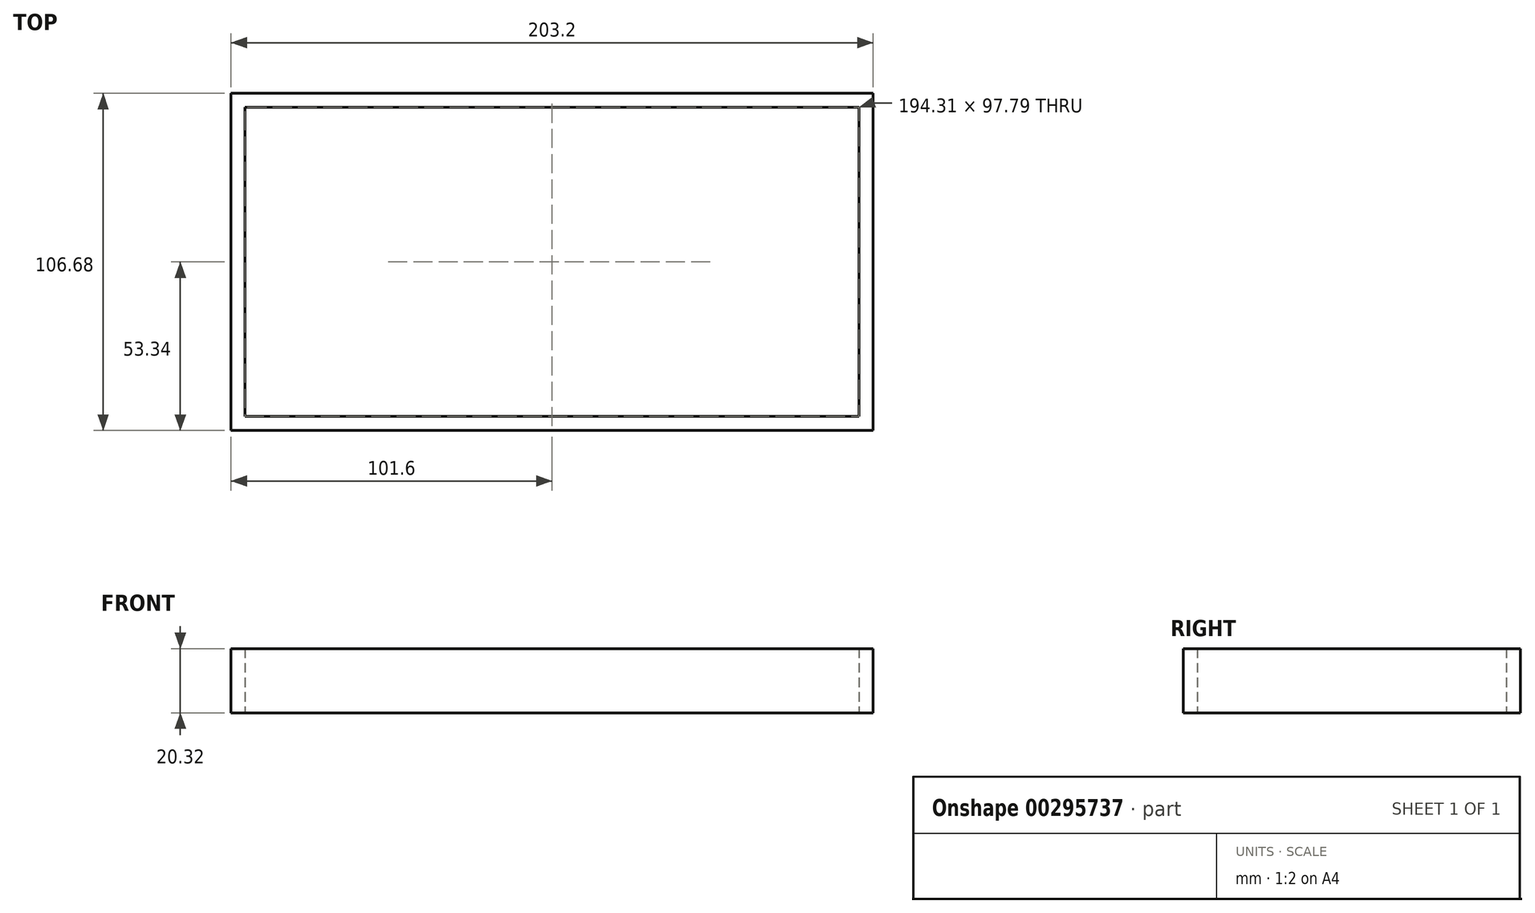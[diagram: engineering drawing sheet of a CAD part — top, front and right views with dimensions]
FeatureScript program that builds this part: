
annotation { "Feature Type Name" : "Feature", "Feature Type Description" : "" }
export const myFeature = defineFeature(function(context is Context, id is Id, definition is map)
    precondition{}
    {
        {
            var Q0;
            Q0=qCreatedBy(makeId("Top.planeOp"),FACE);
            var sketch = newSketch(context, id + "F0", { "sketchPlane" : qUnion([Q0])});
            skLineSegment(sketch, "E0.bottom", {"start": v(-101.6, 53.34) * mm, "end": v(101.6, 53.34) * mm});
            skLineSegment(sketch, "E0.top", {"start": v(-101.6, -53.34) * mm, "end": v(101.6, -53.34) * mm});
            skLineSegment(sketch, "E0.left", {"start": v(-101.6, 53.34) * mm, "end": v(-101.6, -53.34) * mm});
            skLineSegment(sketch, "E0.right", {"start": v(101.6, 53.34) * mm, "end": v(101.6, -53.34) * mm});
            skLineSegment(sketch, "E1.bottom", {"start": v(-97.16, 48.9) * mm, "end": v(97.16, 48.9) * mm});
            skLineSegment(sketch, "E1.top", {"start": v(-97.16, -48.9) * mm, "end": v(97.16, -48.9) * mm});
            skLineSegment(sketch, "E1.left", {"start": v(-97.16, 48.9) * mm, "end": v(-97.16, -48.9) * mm});
            skLineSegment(sketch, "E1.right", {"start": v(97.16, 48.9) * mm, "end": v(97.16, -48.9) * mm});
            skSolve(sketch);
        }
        {
            var Q0;
            Q0=makeQuery(id+"F0.imprint","IMPRINT",FACE,{"disambiguationData":[TD([[makeQuery(id+"F0.imprint","IMPRINT",EDGE,{"derivedFrom":sQuery(id+"F0.wireOp",EDGE,"E0.bottom")}),-1.0]])]});
            extrude(context, id + "F1", {"entities" : qUnion([Q0]), "depth" : 20.32 * mm});
        }
    });
